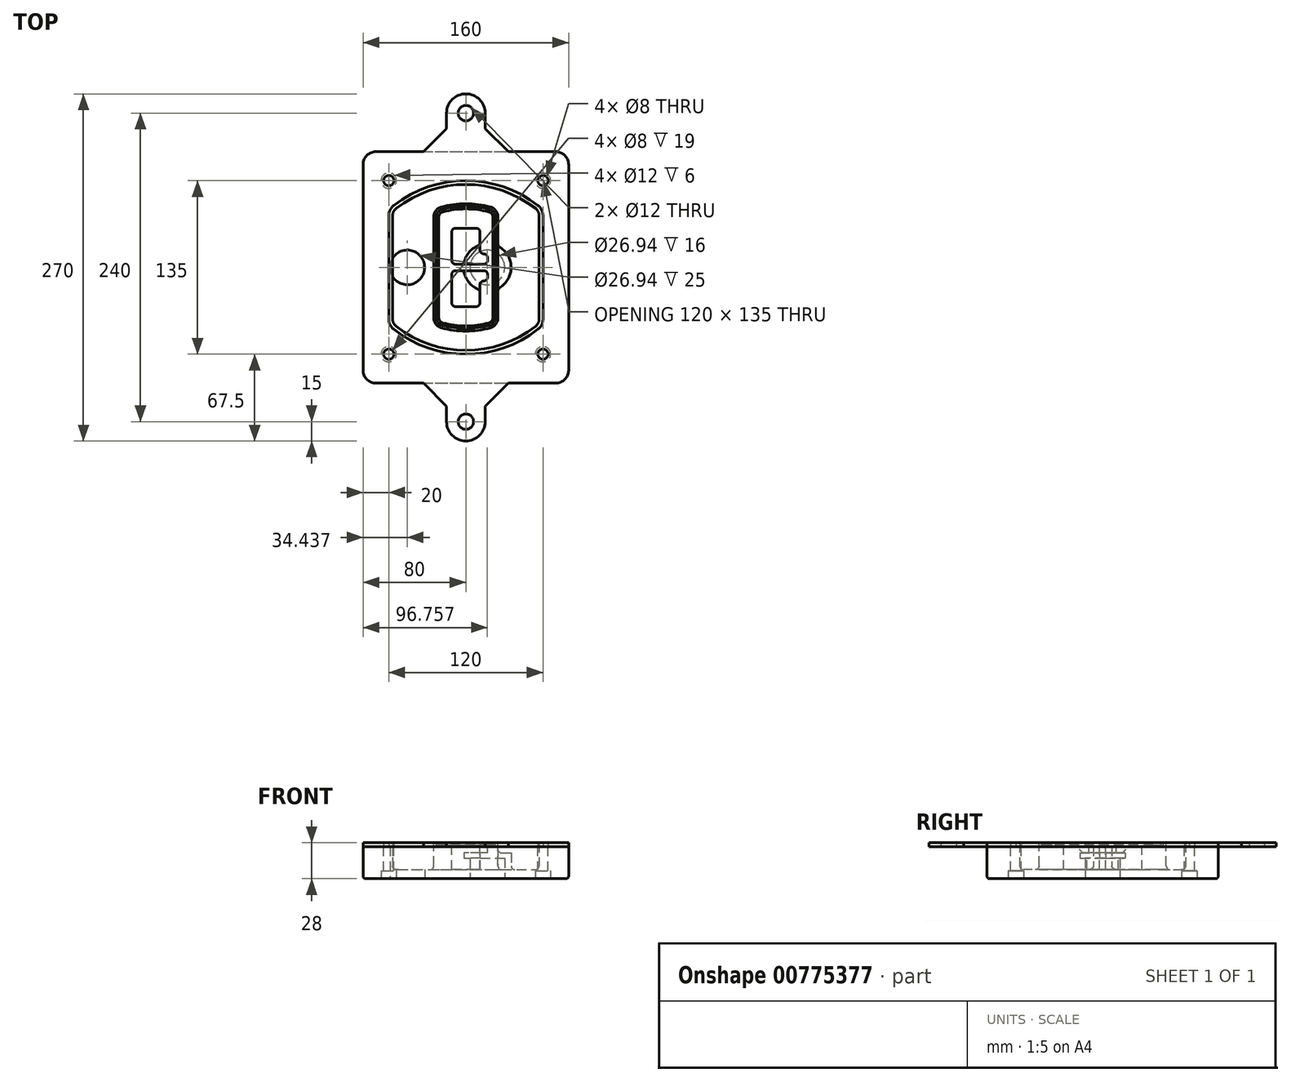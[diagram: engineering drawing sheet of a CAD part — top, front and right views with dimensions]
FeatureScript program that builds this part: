
annotation { "Feature Type Name" : "Feature", "Feature Type Description" : "" }
export const myFeature = defineFeature(function(context is Context, id is Id, definition is map)
    precondition{}
    {
        {
            var Q0;
            Q0=qCreatedBy(makeId("Top.planeOp"),FACE);
            var sketch = newSketch(context, id + "F0", { "sketchPlane" : qUnion([Q0])});
            skPoint(sketch, "E0.rect.middle", {"position": v(0, 0) * mm});
            skLineSegment(sketch, "E1.bottom", {"start": v(-70, -90) * mm, "end": v(70, -90) * mm});
            skLineSegment(sketch, "E1.top", {"start": v(-70, 90) * mm, "end": v(70, 90) * mm});
            skLineSegment(sketch, "E1.left", {"start": v(-80, -80) * mm, "end": v(-80, 80) * mm});
            skLineSegment(sketch, "E1.right", {"start": v(80, -80) * mm, "end": v(80, 80) * mm});
            skLineSegment(sketch, "E2", {"start": v(-80, 90) * mm, "end": v(80, -90) * mm, "construction": true});
            skLineSegment(sketch, "E3", {"start": v(80, 90) * mm, "end": v(-80, -90) * mm, "construction": true});
            skCircle(sketch, "E4", {"center": v(-60, 67.5) * mm, "radius": 4 * mm});
            skCircle(sketch, "E5", {"center": v(60, 67.5) * mm, "radius": 4 * mm});
            skCircle(sketch, "E6", {"center": v(60, -67.5) * mm, "radius": 4 * mm});
            skCircle(sketch, "E7", {"center": v(-60, -67.5) * mm, "radius": 4 * mm});
            skLineSegment(sketch, "E8", {"start": v(-60, 67.5) * mm, "end": v(60, 67.5) * mm, "construction": true});
            skLineSegment(sketch, "E9", {"start": v(60, 67.5) * mm, "end": v(60, -67.5) * mm, "construction": true});
            skLineSegment(sketch, "E10", {"start": v(60, -67.5) * mm, "end": v(-60, -67.5) * mm, "construction": true});
            skLineSegment(sketch, "E11", {"start": v(-60, -67.5) * mm, "end": v(-60, 67.5) * mm, "construction": true});
            skLineSegment(sketch, "E12", {"start": v(-60, 40.3) * mm, "end": v(-60, -40.3) * mm});
            skLineSegment(sketch, "E13", {"start": v(60, 40.3) * mm, "end": v(60, -40.3) * mm});
            skArc(sketch, "E14", {"start": v(56.15, 48.18) * mm, "mid": v(0, 67.5) * mm, "end": v(-56.15, 48.18) * mm});
            skArc(sketch, "E15", {"start": v(-56.15, -48.18) * mm, "mid": v(0, -67.5) * mm, "end": v(56.15, -48.18) * mm});
            skLineSegment(sketch, "E16", {"start": v(-60, 0) * mm, "end": v(60, 0) * mm, "construction": true});
            skPoint(sketch, "E17.visualSharp", {"position": v(-60, -45) * mm});
            skArc(sketch, "E17.filletArc", {"start": v(-60, -40.3) * mm, "mid": v(-58.99, -44.68) * mm, "end": v(-56.15, -48.18) * mm});
            skPoint(sketch, "E18.visualSharp", {"position": v(-60, 45) * mm});
            skArc(sketch, "E18.filletArc", {"start": v(-56.15, 48.18) * mm, "mid": v(-58.99, 44.68) * mm, "end": v(-60, 40.3) * mm});
            skPoint(sketch, "E19.visualSharp", {"position": v(60, 45) * mm});
            skArc(sketch, "E19.filletArc", {"start": v(60, 40.3) * mm, "mid": v(58.99, 44.68) * mm, "end": v(56.15, 48.18) * mm});
            skPoint(sketch, "E20.visualSharp", {"position": v(60, -45) * mm});
            skArc(sketch, "E20.filletArc", {"start": v(56.15, -48.18) * mm, "mid": v(58.99, -44.68) * mm, "end": v(60, -40.3) * mm});
            skPoint(sketch, "E21.visualSharp", {"position": v(-80, 90) * mm});
            skArc(sketch, "E21.filletArc", {"start": v(-70, 90) * mm, "mid": v(-77.07, 87.07) * mm, "end": v(-80, 80) * mm});
            skPoint(sketch, "E22.visualSharp", {"position": v(80, 90) * mm});
            skArc(sketch, "E22.filletArc", {"start": v(80, 80) * mm, "mid": v(77.07, 87.07) * mm, "end": v(70, 90) * mm});
            skPoint(sketch, "E23.visualSharp", {"position": v(80, -90) * mm});
            skArc(sketch, "E23.filletArc", {"start": v(70, -90) * mm, "mid": v(77.07, -87.07) * mm, "end": v(80, -80) * mm});
            skPoint(sketch, "E24.visualSharp", {"position": v(-80, -90) * mm});
            skArc(sketch, "E24.filletArc", {"start": v(-80, -80) * mm, "mid": v(-77.07, -87.07) * mm, "end": v(-70, -90) * mm});
            skArc(sketch, "E25.0", {"start": v(57, 40.3) * mm, "mid": v(56.3, 43.36) * mm, "end": v(54.3, 45.81) * mm});
            skLineSegment(sketch, "E25.1", {"start": v(57, 40.3) * mm, "end": v(57, -40.3) * mm});
            skArc(sketch, "E25.2", {"start": v(54.3, -45.81) * mm, "mid": v(56.3, -43.36) * mm, "end": v(57, -40.3) * mm});
            skArc(sketch, "E25.3", {"start": v(-54.3, -45.81) * mm, "mid": v(0, -64.5) * mm, "end": v(54.3, -45.81) * mm});
            skArc(sketch, "E25.4", {"start": v(-57, -40.3) * mm, "mid": v(-56.3, -43.36) * mm, "end": v(-54.3, -45.81) * mm});
            skArc(sketch, "E25.5", {"start": v(54.3, 45.81) * mm, "mid": v(0, 64.5) * mm, "end": v(-54.3, 45.81) * mm});
            skLineSegment(sketch, "E25.6", {"start": v(-57, 40.3) * mm, "end": v(-57, -40.3) * mm});
            skArc(sketch, "E25.7", {"start": v(-54.3, 45.81) * mm, "mid": v(-56.3, 43.36) * mm, "end": v(-57, 40.3) * mm});
            skArc(sketch, "E26.0", {"start": v(-58.62, 51.33) * mm, "mid": v(-62.58, 46.43) * mm, "end": v(-64, 40.3) * mm});
            skArc(sketch, "E26.1", {"start": v(58.62, 51.33) * mm, "mid": v(0, 71.5) * mm, "end": v(-58.62, 51.33) * mm});
            skArc(sketch, "E26.2", {"start": v(64, 40.3) * mm, "mid": v(62.58, 46.43) * mm, "end": v(58.62, 51.33) * mm});
            skLineSegment(sketch, "E26.3", {"start": v(64, 40.3) * mm, "end": v(64, -40.3) * mm});
            skArc(sketch, "E26.4", {"start": v(58.62, -51.33) * mm, "mid": v(62.58, -46.43) * mm, "end": v(64, -40.3) * mm});
            skLineSegment(sketch, "E26.5", {"start": v(-64, 40.3) * mm, "end": v(-64, -40.3) * mm});
            skArc(sketch, "E26.6", {"start": v(-58.62, -51.33) * mm, "mid": v(0, -71.5) * mm, "end": v(58.62, -51.33) * mm});
            skArc(sketch, "E26.7", {"start": v(-64, -40.3) * mm, "mid": v(-62.58, -46.43) * mm, "end": v(-58.62, -51.33) * mm});
            skSolve(sketch);
        }
        {
            var Q0;
            Q0=makeQuery(id+"F0.imprint","IMPRINT",FACE,{"disambiguationData":[TD([[makeQuery(id+"F0.imprint","IMPRINT",EDGE,{"derivedFrom":sQuery(id+"F0.wireOp",EDGE,"E1.bottom")}),1.0]])]});
            var Q1;
            Q1=makeQuery(id+"F0.imprint","IMPRINT",FACE,{"disambiguationData":[TD([[makeQuery(id+"F0.imprint","IMPRINT",EDGE,{"derivedFrom":sQuery(id+"F0.wireOp",EDGE,"E12")}),1.0]])]});
            var Q2;
            Q2=makeQuery(id+"F0.imprint","IMPRINT",FACE,{"disambiguationData":[TD([[makeQuery(id+"F0.imprint","IMPRINT",EDGE,{"derivedFrom":sQuery(id+"F0.wireOp",EDGE,"E25.0")}),1.0]])]});
            var Q3;
            Q3=makeQuery(id+"F0.imprint","IMPRINT",FACE,{"disambiguationData":[TD([[makeQuery(id+"F0.imprint","IMPRINT",EDGE,{"derivedFrom":sQuery(id+"F0.wireOp",EDGE,"E12")}),-1.0]])]});
            extrude(context, id + "F1", {"entities" : qUnion([Q0, Q1, Q2, Q3]), "oppositeDirection" : true, "depth" : 25 * mm});
        }
        {
            var Q0;
            Q0=makeQuery(id+"F0.imprint","IMPRINT",FACE,{"disambiguationData":[TD([[makeQuery(id+"F0.imprint","IMPRINT",EDGE,{"derivedFrom":sQuery(id+"F0.wireOp",EDGE,"E12")}),1.0]])]});
            extrude(context, id + "F2", {"entities" : qUnion([Q0]), "operationType" : NewBodyOperationType.ADD, "depth" : 3 * mm});
        }
        {
            var Q0;
            Q0=makeQuery(id+"F0.imprint","IMPRINT",FACE,{"disambiguationData":[TD([[makeQuery(id+"F0.imprint","IMPRINT",EDGE,{"derivedFrom":sQuery(id+"F0.wireOp",EDGE,"E25.0")}),1.0]])]});
            extrude(context, id + "F3", {"entities" : qUnion([Q0]), "operationType" : NewBodyOperationType.REMOVE, "oppositeDirection" : true, "depth" : 18 * mm});
        }
        {
            var Q0;
            Q0=makeQuery(id+"F2.opExtrude","CAP_FACE",FACE,{"disambiguationData":[OSD([sQuery(id+"F0.wireOp",EDGE,"E12"),sQuery(id+"F0.wireOp",EDGE,"E13"),sQuery(id+"F0.wireOp",EDGE,"E14"),sQuery(id+"F0.wireOp",EDGE,"E15"),sQuery(id+"F0.wireOp",EDGE,"E17.filletArc"),sQuery(id+"F0.wireOp",EDGE,"E18.filletArc"),sQuery(id+"F0.wireOp",EDGE,"E19.filletArc"),sQuery(id+"F0.wireOp",EDGE,"E20.filletArc"),sQuery(id+"F0.wireOp",EDGE,"E25.0"),sQuery(id+"F0.wireOp",EDGE,"E25.1"),sQuery(id+"F0.wireOp",EDGE,"E25.2"),sQuery(id+"F0.wireOp",EDGE,"E25.3"),sQuery(id+"F0.wireOp",EDGE,"E25.4"),sQuery(id+"F0.wireOp",EDGE,"E25.5"),sQuery(id+"F0.wireOp",EDGE,"E25.6"),sQuery(id+"F0.wireOp",EDGE,"E25.7")])],"isStart":false});
            var sketch = newSketch(context, id + "F4", { "sketchPlane" : qUnion([Q0])});
            skArc(sketch, "E27.0", {"start": v(-19.08, -46.97) * mm, "mid": v(0, -49.5) * mm, "end": v(19.08, -46.97) * mm});
            skArc(sketch, "E28.0", {"start": v(19.08, 46.97) * mm, "mid": v(0, 49.5) * mm, "end": v(-19.08, 46.97) * mm});
            skLineSegment(sketch, "E29", {"start": v(-25, 39.25) * mm, "end": v(-25, -39.25) * mm});
            skLineSegment(sketch, "E30", {"start": v(25, 39.25) * mm, "end": v(25, -39.25) * mm});
            skLineSegment(sketch, "E31", {"start": v(-25, 45.1) * mm, "end": v(25, 45.1) * mm, "construction": true});
            skLineSegment(sketch, "E32", {"start": v(-25, -45.1) * mm, "end": v(25, -45.1) * mm, "construction": true});
            skPoint(sketch, "E33.visualSharp", {"position": v(-25, 45.1) * mm});
            skArc(sketch, "E33.filletArc", {"start": v(-19.08, 46.97) * mm, "mid": v(-23.35, 44.11) * mm, "end": v(-25, 39.25) * mm});
            skPoint(sketch, "E34.visualSharp", {"position": v(25, 45.1) * mm});
            skArc(sketch, "E34.filletArc", {"start": v(25, 39.25) * mm, "mid": v(23.35, 44.11) * mm, "end": v(19.08, 46.97) * mm});
            skPoint(sketch, "E35.visualSharp", {"position": v(25, -45.1) * mm});
            skArc(sketch, "E35.filletArc", {"start": v(19.08, -46.97) * mm, "mid": v(23.35, -44.11) * mm, "end": v(25, -39.25) * mm});
            skPoint(sketch, "E36.visualSharp", {"position": v(-25, -45.1) * mm});
            skArc(sketch, "E36.filletArc", {"start": v(-25, -39.25) * mm, "mid": v(-23.35, -44.11) * mm, "end": v(-19.08, -46.97) * mm});
            skArc(sketch, "E37.0", {"start": v(54.3, 45.81) * mm, "mid": v(0, 64.5) * mm, "end": v(-54.3, 45.81) * mm});
            skArc(sketch, "E37.1", {"start": v(-54.3, 45.81) * mm, "mid": v(-56.3, 43.36) * mm, "end": v(-57, 40.3) * mm});
            skLineSegment(sketch, "E37.2", {"start": v(-57, 40.3) * mm, "end": v(-57, -40.3) * mm});
            skArc(sketch, "E37.3", {"start": v(-57, -40.3) * mm, "mid": v(-56.3, -43.36) * mm, "end": v(-54.3, -45.81) * mm});
            skArc(sketch, "E37.4", {"start": v(-54.3, -45.81) * mm, "mid": v(0, -64.5) * mm, "end": v(54.3, -45.81) * mm});
            skArc(sketch, "E37.5", {"start": v(54.3, -45.81) * mm, "mid": v(56.3, -43.36) * mm, "end": v(57, -40.3) * mm});
            skLineSegment(sketch, "E37.6", {"start": v(57, 40.3) * mm, "end": v(57, -40.3) * mm});
            skArc(sketch, "E37.7", {"start": v(57, 40.3) * mm, "mid": v(56.3, 43.36) * mm, "end": v(54.3, 45.81) * mm});
            skLineSegment(sketch, "E38.0", {"start": v(23, 39.25) * mm, "end": v(23, -39.25) * mm});
            skArc(sketch, "E38.1", {"start": v(18.56, -45.04) * mm, "mid": v(21.76, -42.9) * mm, "end": v(23, -39.25) * mm});
            skArc(sketch, "E38.2", {"start": v(-18.56, -45.04) * mm, "mid": v(0, -47.5) * mm, "end": v(18.56, -45.04) * mm});
            skArc(sketch, "E38.3", {"start": v(-23, -39.25) * mm, "mid": v(-21.76, -42.9) * mm, "end": v(-18.56, -45.04) * mm});
            skLineSegment(sketch, "E38.4", {"start": v(-23, 39.25) * mm, "end": v(-23, -39.25) * mm});
            skArc(sketch, "E38.5", {"start": v(23, 39.25) * mm, "mid": v(21.76, 42.9) * mm, "end": v(18.56, 45.04) * mm});
            skArc(sketch, "E38.6", {"start": v(-18.56, 45.04) * mm, "mid": v(-21.76, 42.9) * mm, "end": v(-23, 39.25) * mm});
            skArc(sketch, "E38.7", {"start": v(18.56, 45.04) * mm, "mid": v(0, 47.5) * mm, "end": v(-18.56, 45.04) * mm});
            skArc(sketch, "E39.0", {"start": v(21, 39.25) * mm, "mid": v(20.18, 41.68) * mm, "end": v(18.04, 43.1) * mm});
            skLineSegment(sketch, "E39.1", {"start": v(21, 39.25) * mm, "end": v(21, -39.25) * mm});
            skArc(sketch, "E39.2", {"start": v(18.04, -43.1) * mm, "mid": v(20.18, -41.68) * mm, "end": v(21, -39.25) * mm});
            skArc(sketch, "E39.3", {"start": v(-18.04, -43.1) * mm, "mid": v(0, -45.5) * mm, "end": v(18.04, -43.1) * mm});
            skArc(sketch, "E39.4", {"start": v(-21, -39.25) * mm, "mid": v(-20.18, -41.68) * mm, "end": v(-18.04, -43.1) * mm});
            skArc(sketch, "E39.5", {"start": v(18.04, 43.1) * mm, "mid": v(0, 45.5) * mm, "end": v(-18.04, 43.1) * mm});
            skLineSegment(sketch, "E39.6", {"start": v(-21, 39.25) * mm, "end": v(-21, -39.25) * mm});
            skArc(sketch, "E39.7", {"start": v(-18.04, 43.1) * mm, "mid": v(-20.18, 41.68) * mm, "end": v(-21, 39.25) * mm});
            skLineSegment(sketch, "E40", {"start": v(-25, 0) * mm, "end": v(25, 0) * mm, "construction": true});
            skLineSegment(sketch, "E41", {"start": v(-11, 5.5) * mm, "end": v(-11, 27.5) * mm});
            skLineSegment(sketch, "E42", {"start": v(-8, 30.5) * mm, "end": v(8, 30.5) * mm});
            skLineSegment(sketch, "E43", {"start": v(11, 27.5) * mm, "end": v(11, 13.5) * mm});
            skLineSegment(sketch, "E44", {"start": v(14, 10.5) * mm, "end": v(14, 10.5) * mm});
            skLineSegment(sketch, "E45", {"start": v(17, 7.5) * mm, "end": v(17, 5.5) * mm});
            skLineSegment(sketch, "E46", {"start": v(14, 2.5) * mm, "end": v(-8, 2.5) * mm});
            skPoint(sketch, "E47.visualSharp", {"position": v(-11, 30.5) * mm});
            skArc(sketch, "E47.filletArc", {"start": v(-8, 30.5) * mm, "mid": v(-10.12, 29.62) * mm, "end": v(-11, 27.5) * mm});
            skPoint(sketch, "E48.visualSharp", {"position": v(11, 30.5) * mm});
            skArc(sketch, "E48.filletArc", {"start": v(11, 27.5) * mm, "mid": v(10.12, 29.62) * mm, "end": v(8, 30.5) * mm});
            skPoint(sketch, "E49.visualSharp", {"position": v(11, 10.5) * mm});
            skArc(sketch, "E49.filletArc", {"start": v(11, 13.5) * mm, "mid": v(11.88, 11.38) * mm, "end": v(14, 10.5) * mm});
            skPoint(sketch, "E50.visualSharp", {"position": v(17, 10.5) * mm});
            skArc(sketch, "E50.filletArc", {"start": v(17, 7.5) * mm, "mid": v(16.12, 9.62) * mm, "end": v(14, 10.5) * mm});
            skPoint(sketch, "E51.visualSharp", {"position": v(17, 2.5) * mm});
            skArc(sketch, "E51.filletArc", {"start": v(14, 2.5) * mm, "mid": v(16.12, 3.38) * mm, "end": v(17, 5.5) * mm});
            skPoint(sketch, "E52.visualSharp", {"position": v(-11, 2.5) * mm});
            skArc(sketch, "E52.filletArc", {"start": v(-11, 5.5) * mm, "mid": v(-10.12, 3.38) * mm, "end": v(-8, 2.5) * mm});
            skLineSegment(sketch, "E53.0.MirrorCS", {"start": v(14, -2.5) * mm, "end": v(-8, -2.5) * mm});
            skArc(sketch, "E54.0.MirrorCS", {"start": v(-11, -5.5) * mm, "mid": v(-10.12, -3.38) * mm, "end": v(-8, -2.5) * mm});
            skLineSegment(sketch, "E55.0.MirrorCS", {"start": v(-11, -5.5) * mm, "end": v(-11, -27.5) * mm});
            skArc(sketch, "E56.0.MirrorCS", {"start": v(-8, -30.5) * mm, "mid": v(-10.12, -29.62) * mm, "end": v(-11, -27.5) * mm});
            skLineSegment(sketch, "E57.0.MirrorCS", {"start": v(-8, -30.5) * mm, "end": v(8, -30.5) * mm});
            skArc(sketch, "E58.0.MirrorCS", {"start": v(11, -27.5) * mm, "mid": v(10.12, -29.62) * mm, "end": v(8, -30.5) * mm});
            skLineSegment(sketch, "E59.0.MirrorCS", {"start": v(11, -27.5) * mm, "end": v(11, -13.5) * mm});
            skArc(sketch, "E60.0.MirrorCS", {"start": v(11, -13.5) * mm, "mid": v(11.88, -11.38) * mm, "end": v(14, -10.5) * mm});
            skArc(sketch, "E61.0.MirrorCS", {"start": v(17, -7.5) * mm, "mid": v(16.12, -9.62) * mm, "end": v(14, -10.5) * mm});
            skLineSegment(sketch, "E62.0.MirrorCS", {"start": v(17, -7.5) * mm, "end": v(17, -5.5) * mm});
            skArc(sketch, "E63.0.MirrorCS", {"start": v(14, -2.5) * mm, "mid": v(16.12, -3.38) * mm, "end": v(17, -5.5) * mm});
            skSolve(sketch);
        }
        {
            var Q0;
            Q0=makeQuery(id+"F4.imprint","IMPRINT",FACE,{"disambiguationData":[TD([[makeQuery(id+"F4.imprint","IMPRINT",EDGE,{"derivedFrom":sQuery(id+"F4.wireOp",EDGE,"E27.0")}),1.0]])]});
            var Q1;
            Q1=makeQuery(id+"F4.imprint","IMPRINT",FACE,{"disambiguationData":[TD([[makeQuery(id+"F4.imprint","IMPRINT",EDGE,{"derivedFrom":sQuery(id+"F4.wireOp",EDGE,"E38.0")}),-1.0]])]});
            var Q2;
            Q2=makeQuery(id+"F4.imprint","IMPRINT",FACE,{"disambiguationData":[TD([[makeQuery(id+"F4.imprint","IMPRINT",EDGE,{"derivedFrom":sQuery(id+"F4.wireOp",EDGE,"E39.0")}),1.0]])]});
            extrude(context, id + "F5", {"entities" : qUnion([Q0, Q1, Q2]), "operationType" : NewBodyOperationType.ADD, "endBound" : BoundingType.UP_TO_NEXT, "oppositeDirection" : true, "depth" : 25 * mm});
        }
        {
            var Q0;
            Q0=makeQuery(id+"F4.imprint","IMPRINT",FACE,{"disambiguationData":[TD([[makeQuery(id+"F4.imprint","IMPRINT",EDGE,{"derivedFrom":sQuery(id+"F4.wireOp",EDGE,"E38.0")}),-1.0]])]});
            extrude(context, id + "F6", {"entities" : qUnion([Q0]), "operationType" : NewBodyOperationType.REMOVE, "oppositeDirection" : true, "depth" : 2 * mm});
        }
        {
            var Q0;
            Q0=makeQuery(id+"F1.opExtrude","CAP_FACE",FACE,{"disambiguationData":[OSD([sQuery(id+"F0.wireOp",EDGE,"E1.bottom"),sQuery(id+"F0.wireOp",EDGE,"E1.top"),sQuery(id+"F0.wireOp",EDGE,"E1.left"),sQuery(id+"F0.wireOp",EDGE,"E1.right"),sQuery(id+"F0.wireOp",EDGE,"E4"),sQuery(id+"F0.wireOp",EDGE,"E5"),sQuery(id+"F0.wireOp",EDGE,"E6"),sQuery(id+"F0.wireOp",EDGE,"E7"),sQuery(id+"F0.wireOp",EDGE,"E21.filletArc"),sQuery(id+"F0.wireOp",EDGE,"E22.filletArc"),sQuery(id+"F0.wireOp",EDGE,"E23.filletArc"),sQuery(id+"F0.wireOp",EDGE,"E24.filletArc")])],"isStart":false});
            var sketch = newSketch(context, id + "F7", { "sketchPlane" : qUnion([Q0])});
            skCircle(sketch, "E64", {"center": v(16.76, 0) * mm, "radius": 13.47 * mm});
            skCircle(sketch, "E65", {"center": v(-45.56, 0) * mm, "radius": 13.47 * mm});
            skLineSegment(sketch, "E66", {"start": v(80, 0) * mm, "end": v(-80, 0) * mm});
            skCircle(sketch, "E67", {"center": v(16.76, 0) * mm, "radius": 18.47 * mm});
            skCircle(sketch, "E68", {"center": v(60, -67.5) * mm, "radius": 6 * mm});
            skCircle(sketch, "E69", {"center": v(-60, -67.5) * mm, "radius": 6 * mm});
            skCircle(sketch, "E70", {"center": v(-60, 67.5) * mm, "radius": 6 * mm});
            skCircle(sketch, "E71", {"center": v(60, 67.5) * mm, "radius": 6 * mm});
            skSolve(sketch);
        }
        {
            var Q0;
            {var subQ1=sQuery(id+"F7.wireOp",EDGE,"E66");var subQ4=sQuery(id+"F7.wireOp",EDGE,"E64");var subQ6=makeQuery(id+"F7.imprint","INTERSECT",VERTEX,{"disambiguationData":[OD(0.0)],"derivedFrom":[subQ4,subQ1]});Q0=makeQuery(id+"F7.imprint","IMPRINT",FACE,{"disambiguationData":[TD([[makeQuery(id+"F7.imprint","IMPRINT",EDGE,{"disambiguationData":[TD([[subQ6,-1.0]])],"derivedFrom":subQ4}),-1.0]])]});}
            var Q1;
            {var subQ0=sQuery(id+"F7.wireOp",EDGE,"E66");var subQ1=sQuery(id+"F7.wireOp",EDGE,"E64");var subQ3=makeQuery(id+"F7.imprint","INTERSECT",VERTEX,{"disambiguationData":[OD(0.0)],"derivedFrom":[subQ1,subQ0]});Q1=makeQuery(id+"F7.imprint","IMPRINT",FACE,{"disambiguationData":[TD([[makeQuery(id+"F7.imprint","IMPRINT",EDGE,{"disambiguationData":[TD([[subQ3,-1.0]])],"derivedFrom":subQ1}),1.0]])]});}
            var Q2;
            {var subQ0=sQuery(id+"F7.wireOp",EDGE,"E66");var subQ1=sQuery(id+"F7.wireOp",EDGE,"E64");var subQ3=makeQuery(id+"F7.imprint","INTERSECT",VERTEX,{"disambiguationData":[OD(0.0)],"derivedFrom":[subQ1,subQ0]});Q2=makeQuery(id+"F7.imprint","IMPRINT",FACE,{"disambiguationData":[TD([[makeQuery(id+"F7.imprint","IMPRINT",EDGE,{"disambiguationData":[TD([[subQ3,1.0]])],"derivedFrom":subQ1}),1.0]])]});}
            var Q3;
            {var subQ1=sQuery(id+"F7.wireOp",EDGE,"E66");var subQ4=sQuery(id+"F7.wireOp",EDGE,"E64");var subQ6=makeQuery(id+"F7.imprint","INTERSECT",VERTEX,{"disambiguationData":[OD(0.0)],"derivedFrom":[subQ4,subQ1]});Q3=makeQuery(id+"F7.imprint","IMPRINT",FACE,{"disambiguationData":[TD([[makeQuery(id+"F7.imprint","IMPRINT",EDGE,{"disambiguationData":[TD([[subQ6,1.0]])],"derivedFrom":subQ4}),-1.0]])]});}
            extrude(context, id + "F8", {"entities" : qUnion([Q0, Q1, Q2, Q3]), "operationType" : NewBodyOperationType.ADD, "oppositeDirection" : true, "depth" : 20 * mm});
        }
        {
            var Q0;
            {var subQ0=sQuery(id+"F7.wireOp",EDGE,"E66");var subQ1=sQuery(id+"F7.wireOp",EDGE,"E64");var subQ3=makeQuery(id+"F7.imprint","INTERSECT",VERTEX,{"disambiguationData":[OD(0.0)],"derivedFrom":[subQ1,subQ0]});Q0=makeQuery(id+"F7.imprint","IMPRINT",FACE,{"disambiguationData":[TD([[makeQuery(id+"F7.imprint","IMPRINT",EDGE,{"disambiguationData":[TD([[subQ3,-1.0]])],"derivedFrom":subQ1}),1.0]])]});}
            var Q1;
            {var subQ0=sQuery(id+"F7.wireOp",EDGE,"E66");var subQ1=sQuery(id+"F7.wireOp",EDGE,"E64");var subQ3=makeQuery(id+"F7.imprint","INTERSECT",VERTEX,{"disambiguationData":[OD(0.0)],"derivedFrom":[subQ1,subQ0]});Q1=makeQuery(id+"F7.imprint","IMPRINT",FACE,{"disambiguationData":[TD([[makeQuery(id+"F7.imprint","IMPRINT",EDGE,{"disambiguationData":[TD([[subQ3,1.0]])],"derivedFrom":subQ1}),1.0]])]});}
            extrude(context, id + "F9", {"entities" : qUnion([Q0, Q1]), "operationType" : NewBodyOperationType.REMOVE, "oppositeDirection" : true, "depth" : 16 * mm});
        }
        {
            var Q0;
            {var subQ0=sQuery(id+"F7.wireOp",EDGE,"E66");var subQ1=sQuery(id+"F7.wireOp",EDGE,"E65");var subQ3=makeQuery(id+"F7.imprint","INTERSECT",VERTEX,{"disambiguationData":[OD(0.0)],"derivedFrom":[subQ1,subQ0]});Q0=makeQuery(id+"F7.imprint","IMPRINT",FACE,{"disambiguationData":[TD([[makeQuery(id+"F7.imprint","IMPRINT",EDGE,{"disambiguationData":[TD([[subQ3,-1.0]])],"derivedFrom":subQ1}),1.0]])]});}
            var Q1;
            {var subQ0=sQuery(id+"F7.wireOp",EDGE,"E66");var subQ1=sQuery(id+"F7.wireOp",EDGE,"E65");var subQ3=makeQuery(id+"F7.imprint","INTERSECT",VERTEX,{"disambiguationData":[OD(0.0)],"derivedFrom":[subQ1,subQ0]});Q1=makeQuery(id+"F7.imprint","IMPRINT",FACE,{"disambiguationData":[TD([[makeQuery(id+"F7.imprint","IMPRINT",EDGE,{"disambiguationData":[TD([[subQ3,1.0]])],"derivedFrom":subQ1}),1.0]])]});}
            extrude(context, id + "F10", {"entities" : qUnion([Q0, Q1]), "operationType" : NewBodyOperationType.REMOVE, "oppositeDirection" : true, "depth" : 25 * mm});
        }
        {
            var Q0;
            Q0=makeQuery(id+"F7.imprint","IMPRINT",FACE,{"disambiguationData":[TD([[makeQuery(id+"F7.imprint","IMPRINT",EDGE,{"derivedFrom":sQuery(id+"F7.wireOp",EDGE,"E68")}),1.0]])]});
            var Q1;
            Q1=makeQuery(id+"F7.imprint","IMPRINT",FACE,{"disambiguationData":[TD([[makeQuery(id+"F7.imprint","IMPRINT",EDGE,{"derivedFrom":makeQuery(id+"F1.opExtrude","CAP_EDGE",EDGE,{"disambiguationData":[OSD([sQuery(id+"F0.wireOp",EDGE,"E5")])],"isStart":false})}),-1.0]])]});
            var Q2;
            Q2=makeQuery(id+"F7.imprint","IMPRINT",FACE,{"disambiguationData":[TD([[makeQuery(id+"F7.imprint","IMPRINT",EDGE,{"derivedFrom":sQuery(id+"F7.wireOp",EDGE,"E69")}),1.0]])]});
            var Q3;
            Q3=makeQuery(id+"F7.imprint","IMPRINT",FACE,{"disambiguationData":[TD([[makeQuery(id+"F7.imprint","IMPRINT",EDGE,{"derivedFrom":makeQuery(id+"F1.opExtrude","CAP_EDGE",EDGE,{"disambiguationData":[OSD([sQuery(id+"F0.wireOp",EDGE,"E4")])],"isStart":false})}),-1.0]])]});
            var Q4;
            Q4=makeQuery(id+"F7.imprint","IMPRINT",FACE,{"disambiguationData":[TD([[makeQuery(id+"F7.imprint","IMPRINT",EDGE,{"derivedFrom":sQuery(id+"F7.wireOp",EDGE,"E70")}),1.0]])]});
            var Q5;
            Q5=makeQuery(id+"F7.imprint","IMPRINT",FACE,{"disambiguationData":[TD([[makeQuery(id+"F7.imprint","IMPRINT",EDGE,{"derivedFrom":makeQuery(id+"F1.opExtrude","CAP_EDGE",EDGE,{"disambiguationData":[OSD([sQuery(id+"F0.wireOp",EDGE,"E7")])],"isStart":false})}),-1.0]])]});
            var Q6;
            Q6=makeQuery(id+"F7.imprint","IMPRINT",FACE,{"disambiguationData":[TD([[makeQuery(id+"F7.imprint","IMPRINT",EDGE,{"derivedFrom":sQuery(id+"F7.wireOp",EDGE,"E71")}),1.0]])]});
            var Q7;
            Q7=makeQuery(id+"F7.imprint","IMPRINT",FACE,{"disambiguationData":[TD([[makeQuery(id+"F7.imprint","IMPRINT",EDGE,{"derivedFrom":makeQuery(id+"F1.opExtrude","CAP_EDGE",EDGE,{"disambiguationData":[OSD([sQuery(id+"F0.wireOp",EDGE,"E6")])],"isStart":false})}),-1.0]])]});
            extrude(context, id + "F11", {"entities" : qUnion([Q0, Q1, Q2, Q3, Q4, Q5, Q6, Q7]), "operationType" : NewBodyOperationType.REMOVE, "oppositeDirection" : true, "depth" : 6 * mm});
        }
        {
            var Q0;
            Q0=makeQuery(id+"F9.boolean.opBoolean","COPY",FACE,{"derivedFrom":makeQuery(id+"F9.opExtrude","CAP_FACE",FACE,{"disambiguationData":[OSD([sQuery(id+"F7.wireOp",EDGE,"E64")])],"isStart":false})});
            var sketch = newSketch(context, id + "F12", { "sketchPlane" : qUnion([Q0])});
            skArc(sketch, "E72.0", {"start": v(11, 17.55) * mm, "mid": v(2.57, 11.82) * mm, "end": v(-1.54, 2.5) * mm});
            skArc(sketch, "E72.1", {"start": v(-1.54, -2.5) * mm, "mid": v(2.57, -11.82) * mm, "end": v(11, -17.55) * mm});
            skLineSegment(sketch, "E73", {"start": v(-1.54, -2.5) * mm, "end": v(14, -2.5) * mm});
            skLineSegment(sketch, "E74.0", {"start": v(14, 2.5) * mm, "end": v(-1.54, 2.5) * mm});
            skArc(sketch, "E74.1", {"start": v(14, 2.5) * mm, "mid": v(16.12, 3.38) * mm, "end": v(17, 5.5) * mm});
            skLineSegment(sketch, "E74.2", {"start": v(17, 7.5) * mm, "end": v(17, 5.5) * mm});
            skArc(sketch, "E74.3", {"start": v(17, 7.5) * mm, "mid": v(16.12, 9.62) * mm, "end": v(14, 10.5) * mm});
            skArc(sketch, "E74.4", {"start": v(11, 13.5) * mm, "mid": v(11.88, 11.38) * mm, "end": v(14, 10.5) * mm});
            skLineSegment(sketch, "E74.5", {"start": v(11, 17.55) * mm, "end": v(11, 13.5) * mm});
            skLineSegment(sketch, "E74.7", {"start": v(14, -2.5) * mm, "end": v(-1.54, -2.5) * mm});
            skArc(sketch, "E74.8", {"start": v(14, -2.5) * mm, "mid": v(16.12, -3.38) * mm, "end": v(17, -5.5) * mm});
            skLineSegment(sketch, "E74.9", {"start": v(17, -7.5) * mm, "end": v(17, -5.5) * mm});
            skArc(sketch, "E74.10", {"start": v(17, -7.5) * mm, "mid": v(16.12, -9.62) * mm, "end": v(14, -10.5) * mm});
            skArc(sketch, "E74.11", {"start": v(11, -13.5) * mm, "mid": v(11.88, -11.38) * mm, "end": v(14, -10.5) * mm});
            skLineSegment(sketch, "E74.12", {"start": v(11, -17.55) * mm, "end": v(11, -13.5) * mm});
            skPoint(sketch, "E75.orphan", {"position": v(11, -27.5) * mm});
            skPoint(sketch, "E76.orphan", {"position": v(-8, -2.5) * mm});
            skPoint(sketch, "E77.orphan", {"position": v(-8, 2.5) * mm});
            skPoint(sketch, "E78.orphan", {"position": v(11, 27.5) * mm});
            skSolve(sketch);
        }
        {
            var Q0;
            {var subQ7=sQuery(id+"F12.wireOp",EDGE,"E72.0");var subQ14=sQuery(id+"F12.wireOp",EDGE,"E72.1");var subQ16=sQuery(id+"F12.wireOp",EDGE,"E74.1");var subQ18=sQuery(id+"F12.wireOp",EDGE,"E74.8");Q0=qUnion([makeQuery(id+"F12.imprint","IMPRINT",FACE,{"disambiguationData":[TD([[makeQuery(id+"F12.imprint","IMPRINT",EDGE,{"derivedFrom":subQ7}),1.0]])]}),makeQuery(id+"F12.imprint","IMPRINT",FACE,{"disambiguationData":[TD([[makeQuery(id+"F12.imprint","IMPRINT",EDGE,{"derivedFrom":subQ14}),1.0]])]}),makeQuery(id+"F12.imprint","IMPRINT",FACE,{"disambiguationData":[TD([[makeQuery(id+"F12.imprint","IMPRINT",EDGE,{"derivedFrom":subQ16}),1.0]])]}),makeQuery(id+"F12.imprint","IMPRINT",FACE,{"disambiguationData":[TD([[makeQuery(id+"F12.imprint","IMPRINT",EDGE,{"derivedFrom":subQ18}),-1.0]])]})]);}
            var Q1;
            Q1=makeQuery(id+"F5.boolean.opBoolean","SPLIT",FACE,{"disambiguationData":[TD([makeQuery(id+"F5.opExtrude","SWEPT_FACE",FACE,{"disambiguationData":[OSD([sQuery(id+"F4.wireOp",EDGE,"E41")])]})])],"derivedFrom":makeQuery(id+"F3.boolean.opBoolean","COPY",FACE,{"derivedFrom":makeQuery(id+"F3.opExtrude","CAP_FACE",FACE,{"disambiguationData":[OSD([sQuery(id+"F0.wireOp",EDGE,"E25.0"),sQuery(id+"F0.wireOp",EDGE,"E25.1"),sQuery(id+"F0.wireOp",EDGE,"E25.2"),sQuery(id+"F0.wireOp",EDGE,"E25.3"),sQuery(id+"F0.wireOp",EDGE,"E25.4"),sQuery(id+"F0.wireOp",EDGE,"E25.5"),sQuery(id+"F0.wireOp",EDGE,"E25.6"),sQuery(id+"F0.wireOp",EDGE,"E25.7")])],"isStart":false})})});
            extrude(context, id + "F13", {"entities" : qUnion([Q0]), "operationType" : NewBodyOperationType.REMOVE, "endBound" : BoundingType.UP_TO_SURFACE, "endBoundEntityFace" : qUnion([Q1]), "depth" : 25 * mm});
        }
        {
            var Q0;
            Q0=makeQuery(id+"F3.boolean.opBoolean","COPY",EDGE,{"derivedFrom":makeQuery(id+"F3.opExtrude","CAP_EDGE",EDGE,{"disambiguationData":[OSD([sQuery(id+"F0.wireOp",EDGE,"E25.6")])],"isStart":false})});
            var Q1;
            Q1=makeQuery(id+"F8.boolean.opBoolean","INTERSECT",EDGE,{"derivedFrom":[makeQuery(id+"F5.opExtrude","SWEPT_FACE",FACE,{"disambiguationData":[OSD([sQuery(id+"F4.wireOp",EDGE,"E30")])]}),makeQuery(id+"F8.opExtrude","CAP_FACE",FACE,{"disambiguationData":[OSD([sQuery(id+"F7.wireOp",EDGE,"E67")])],"isStart":false})]});
            var Q2;
            Q2=makeQuery(id+"F8.boolean.opBoolean","INTERSECT",EDGE,{"disambiguationData":[OD(1.0)],"derivedFrom":[makeQuery(id+"F5.opExtrude","SWEPT_FACE",FACE,{"disambiguationData":[OSD([sQuery(id+"F4.wireOp",EDGE,"E30")])]}),makeQuery(id+"F8.opExtrude","SWEPT_FACE",FACE,{"disambiguationData":[OSD([sQuery(id+"F7.wireOp",EDGE,"E67")])]})]});
            var Q3;
            {var subQ0=sQuery(id+"F4.wireOp",EDGE,"E30");Q3=makeQuery(id+"F8.boolean.opBoolean","SPLIT",EDGE,{"disambiguationData":[TD([makeQuery(id+"F5.opExtrude","SWEPT_FACE",FACE,{"disambiguationData":[OSD([sQuery(id+"F4.wireOp",EDGE,"E35.filletArc")])]})])],"derivedFrom":makeQuery(id+"F5.opExtrude","CAP_EDGE",EDGE,{"disambiguationData":[OSD([subQ0])],"isStart":false})});}
            var Q4;
            {var subQ0=sQuery(id+"F0.wireOp",EDGE,"E25.7");var subQ1=sQuery(id+"F0.wireOp",EDGE,"E25.1");var subQ2=sQuery(id+"F0.wireOp",EDGE,"E25.6");var subQ3=sQuery(id+"F0.wireOp",EDGE,"E25.5");var subQ4=sQuery(id+"F0.wireOp",EDGE,"E25.4");var subQ5=sQuery(id+"F0.wireOp",EDGE,"E25.0");var subQ6=sQuery(id+"F0.wireOp",EDGE,"E25.2");var subQ7=sQuery(id+"F0.wireOp",EDGE,"E25.3");Q4=makeQuery(id+"F8.boolean.opBoolean","INTERSECT",EDGE,{"derivedFrom":[makeQuery(id+"F5.boolean.opBoolean","SPLIT",FACE,{"disambiguationData":[TD([makeQuery(id+"F2.opExtrude","SWEPT_FACE",FACE,{"disambiguationData":[OSD([subQ5])]})])],"derivedFrom":makeQuery(id+"F3.boolean.opBoolean","COPY",FACE,{"derivedFrom":makeQuery(id+"F3.opExtrude","CAP_FACE",FACE,{"disambiguationData":[OSD([subQ5,subQ1,subQ6,subQ7,subQ4,subQ3,subQ2,subQ0])],"isStart":false})})}),makeQuery(id+"F8.opExtrude","SWEPT_FACE",FACE,{"disambiguationData":[OSD([sQuery(id+"F7.wireOp",EDGE,"E67")])]})]});}
            var Q5;
            Q5=makeQuery(id+"F8.boolean.opBoolean","INTERSECT",EDGE,{"disambiguationData":[OD(0.0)],"derivedFrom":[makeQuery(id+"F5.opExtrude","SWEPT_FACE",FACE,{"disambiguationData":[OSD([sQuery(id+"F4.wireOp",EDGE,"E30")])]}),makeQuery(id+"F8.opExtrude","SWEPT_FACE",FACE,{"disambiguationData":[OSD([sQuery(id+"F7.wireOp",EDGE,"E67")])]})]});
            fillet(context, id + "F14", {"entities" : qUnion([Q0, Q1, Q2, Q3, Q4, Q5]), "radius" : 3 * mm, "tangentPropagation" : true, "allowEdgeOverflow" : false});
        }
        {
            var Q0;
            Q0=makeQuery(id+"F1.opExtrude","CAP_EDGE",EDGE,{"disambiguationData":[OSD([sQuery(id+"F0.wireOp",EDGE,"E1.bottom")])],"isStart":false});
            fillet(context, id + "F15", {"entities" : qUnion([Q0]), "radius" : 2 * mm, "tangentPropagation" : true, "allowEdgeOverflow" : false});
        }
        {
            var Q0;
            {var subQ0=sQuery(id+"F0.wireOp",EDGE,"E21.filletArc");var subQ1=sQuery(id+"F0.wireOp",EDGE,"E7");var subQ2=sQuery(id+"F0.wireOp",EDGE,"E6");var subQ3=sQuery(id+"F0.wireOp",EDGE,"E5");var subQ4=sQuery(id+"F0.wireOp",EDGE,"E4");var subQ5=sQuery(id+"F0.wireOp",EDGE,"E22.filletArc");var subQ6=sQuery(id+"F0.wireOp",EDGE,"E1.bottom");var subQ7=sQuery(id+"F0.wireOp",EDGE,"E1.right");var subQ8=sQuery(id+"F0.wireOp",EDGE,"E1.top");var subQ9=sQuery(id+"F0.wireOp",EDGE,"E1.left");var subQ10=sQuery(id+"F0.wireOp",EDGE,"E23.filletArc");var subQ11=sQuery(id+"F0.wireOp",EDGE,"E24.filletArc");Q0=makeQuery(id+"F2.boolean.opBoolean","SPLIT",FACE,{"disambiguationData":[TD([makeQuery(id+"F1.opExtrude","SWEPT_FACE",FACE,{"disambiguationData":[OSD([subQ6])]})])],"derivedFrom":makeQuery(id+"F1.opExtrude","CAP_FACE",FACE,{"disambiguationData":[OSD([subQ6,subQ8,subQ9,subQ7,subQ4,subQ3,subQ2,subQ1,subQ0,subQ5,subQ10,subQ11])],"isStart":true})});}
            var sketch = newSketch(context, id + "F16", { "sketchPlane" : qUnion([Q0])});
            skLineSegment(sketch, "E79.1", {"start": v(-60, 40.3) * mm, "end": v(-60, -40.3) * mm});
            skArc(sketch, "E79.2", {"start": v(-56.15, 48.18) * mm, "mid": v(-58.99, 44.68) * mm, "end": v(-60, 40.3) * mm});
            skArc(sketch, "E79.3", {"start": v(56.15, 48.18) * mm, "mid": v(0, 67.5) * mm, "end": v(-56.15, 48.18) * mm});
            skArc(sketch, "E79.4", {"start": v(60, 40.3) * mm, "mid": v(58.99, 44.68) * mm, "end": v(56.15, 48.18) * mm});
            skLineSegment(sketch, "E79.5", {"start": v(60, 40.3) * mm, "end": v(60, -40.3) * mm});
            skArc(sketch, "E79.6", {"start": v(56.15, -48.18) * mm, "mid": v(58.99, -44.68) * mm, "end": v(60, -40.3) * mm});
            skArc(sketch, "E79.7", {"start": v(-56.15, -48.18) * mm, "mid": v(0, -67.5) * mm, "end": v(56.15, -48.18) * mm});
            skArc(sketch, "E79.8", {"start": v(-60, -40.3) * mm, "mid": v(-58.99, -44.68) * mm, "end": v(-56.15, -48.18) * mm});
            skLineSegment(sketch, "E79.9", {"start": v(-80, -80) * mm, "end": v(-80, 80) * mm});
            skArc(sketch, "E79.10", {"start": v(-70, 90) * mm, "mid": v(-77.07, 87.07) * mm, "end": v(-80, 80) * mm});
            skLineSegment(sketch, "E79.11", {"start": v(-70, 90) * mm, "end": v(70, 90) * mm});
            skArc(sketch, "E79.12", {"start": v(80, 80) * mm, "mid": v(77.07, 87.07) * mm, "end": v(70, 90) * mm});
            skLineSegment(sketch, "E79.13", {"start": v(80, -80) * mm, "end": v(80, 80) * mm});
            skArc(sketch, "E79.14", {"start": v(70, -90) * mm, "mid": v(77.07, -87.07) * mm, "end": v(80, -80) * mm});
            skLineSegment(sketch, "E79.15", {"start": v(-70, -90) * mm, "end": v(70, -90) * mm});
            skArc(sketch, "E79.16", {"start": v(-80, -80) * mm, "mid": v(-77.07, -87.07) * mm, "end": v(-70, -90) * mm});
            skLineSegment(sketch, "E80.0.0", {"start": v(70, 90) * mm, "end": v(-70, 90) * mm});
            skLineSegment(sketch, "E80.0.2", {"start": v(-80, 80) * mm, "end": v(-80, -80) * mm});
            skLineSegment(sketch, "E81.0.0", {"start": v(60, -40.3) * mm, "end": v(60, 40.3) * mm});
            skCircle(sketch, "E82.0", {"center": v(-60, 67.5) * mm, "radius": 4 * mm});
            skCircle(sketch, "E83.0", {"center": v(60, 67.5) * mm, "radius": 4 * mm});
            skCircle(sketch, "E84.0", {"center": v(60, -67.5) * mm, "radius": 4 * mm});
            skCircle(sketch, "E85.0", {"center": v(-60, -67.5) * mm, "radius": 4 * mm});
            skPoint(sketch, "E86.0", {"position": v(0, 0) * mm});
            skLineSegment(sketch, "E87", {"start": v(0, 90) * mm, "end": v(0, 120) * mm, "construction": true});
            skCircle(sketch, "E88", {"center": v(0, 120) * mm, "radius": 6 * mm});
            skArc(sketch, "E89", {"start": v(15, 120) * mm, "mid": v(0, 135) * mm, "end": v(-15, 120) * mm});
            skLineSegment(sketch, "E90", {"start": v(15, 120) * mm, "end": v(15, 108) * mm});
            skLineSegment(sketch, "E91", {"start": v(15, 108) * mm, "end": v(33, 90) * mm});
            skLineSegment(sketch, "E92", {"start": v(-15, 120) * mm, "end": v(-15, 108) * mm});
            skLineSegment(sketch, "E93", {"start": v(-15, 108) * mm, "end": v(-33, 90) * mm});
            skLineSegment(sketch, "E94", {"start": v(80, 0) * mm, "end": v(-80, 0) * mm, "construction": true});
            skLineSegment(sketch, "E95.MirrorCS", {"start": v(15, -120) * mm, "end": v(15, -108) * mm});
            skLineSegment(sketch, "E96.MirrorCS", {"start": v(-15, -120) * mm, "end": v(-15, -108) * mm});
            skLineSegment(sketch, "E97.MirrorCS", {"start": v(-15, -108) * mm, "end": v(-33, -90) * mm});
            skCircle(sketch, "E98.MirrorC", {"center": v(0, -120) * mm, "radius": 6 * mm});
            skArc(sketch, "E99.MirrorCS", {"start": v(15, -120) * mm, "mid": v(0, -135) * mm, "end": v(-15, -120) * mm});
            skLineSegment(sketch, "E100.MirrorCS", {"start": v(0, -90) * mm, "end": v(0, -120) * mm, "construction": true});
            skLineSegment(sketch, "E101.MirrorCS", {"start": v(15, -108) * mm, "end": v(33, -90) * mm});
            skSolve(sketch);
        }
        {
            var Q0;
            Q0 = qSketchRegion(id + "F16", true);
            var Q1;
            Q1=makeQuery(id+"F2.opExtrude","CAP_FACE",FACE,{"disambiguationData":[OSD([sQuery(id+"F0.wireOp",EDGE,"E12"),sQuery(id+"F0.wireOp",EDGE,"E13"),sQuery(id+"F0.wireOp",EDGE,"E14"),sQuery(id+"F0.wireOp",EDGE,"E15"),sQuery(id+"F0.wireOp",EDGE,"E17.filletArc"),sQuery(id+"F0.wireOp",EDGE,"E18.filletArc"),sQuery(id+"F0.wireOp",EDGE,"E19.filletArc"),sQuery(id+"F0.wireOp",EDGE,"E20.filletArc"),sQuery(id+"F0.wireOp",EDGE,"E25.0"),sQuery(id+"F0.wireOp",EDGE,"E25.1"),sQuery(id+"F0.wireOp",EDGE,"E25.2"),sQuery(id+"F0.wireOp",EDGE,"E25.3"),sQuery(id+"F0.wireOp",EDGE,"E25.4"),sQuery(id+"F0.wireOp",EDGE,"E25.5"),sQuery(id+"F0.wireOp",EDGE,"E25.6"),sQuery(id+"F0.wireOp",EDGE,"E25.7")])],"isStart":false});
            extrude(context, id + "F17", {"entities" : qUnion([Q0]), "endBound" : BoundingType.UP_TO_SURFACE, "depth" : 25 * mm, "endBoundEntityFace" : qUnion([Q1]), "offsetDistance" : 25 * mm});
        }
    });
